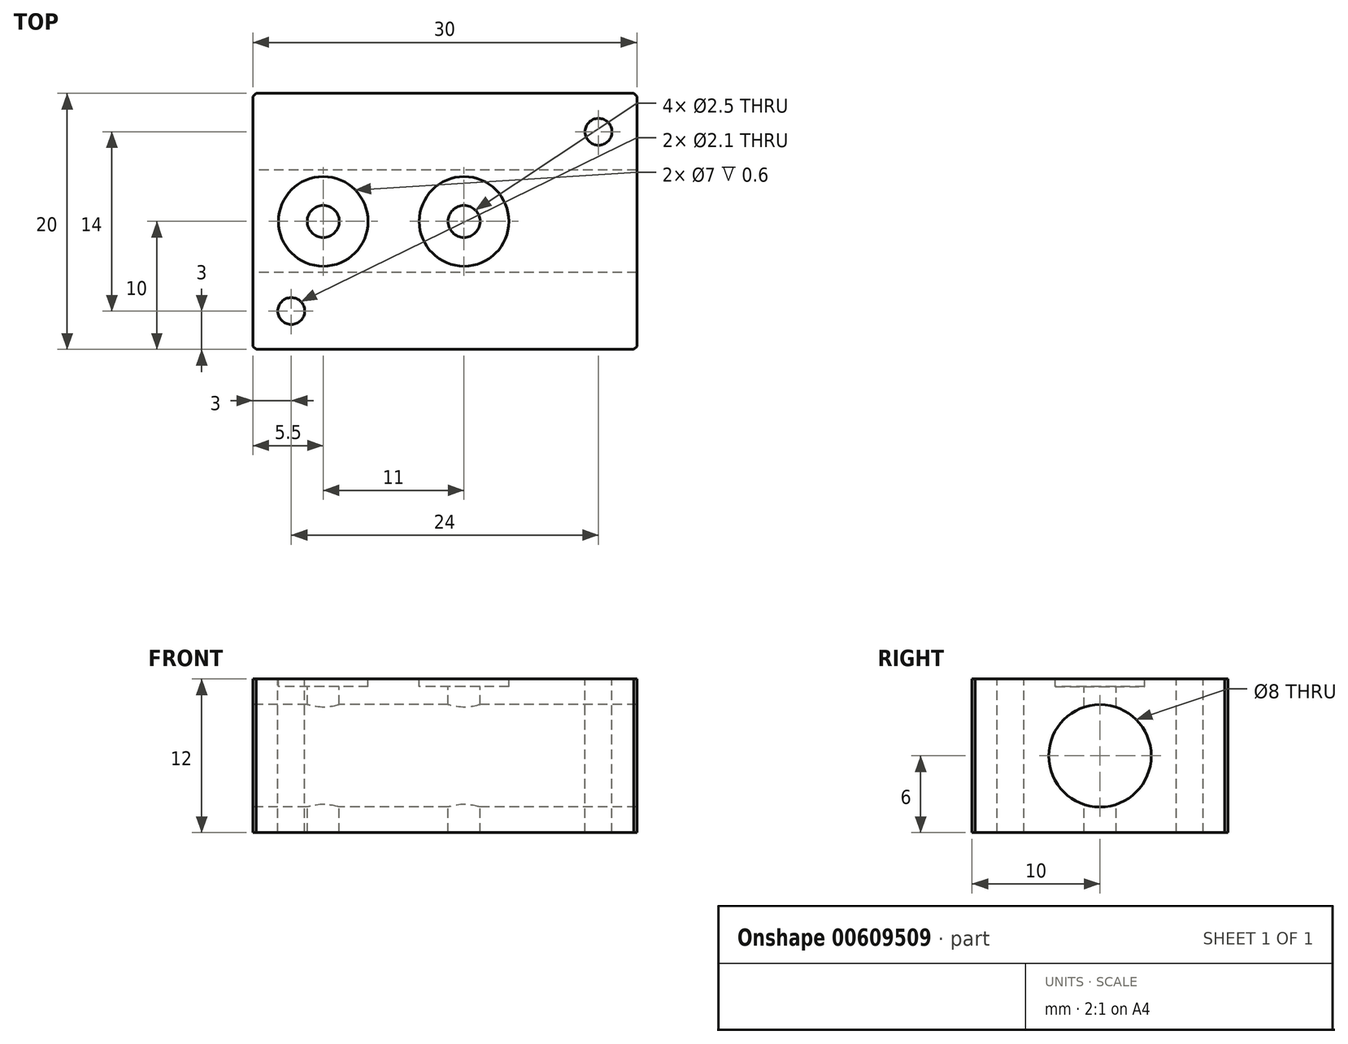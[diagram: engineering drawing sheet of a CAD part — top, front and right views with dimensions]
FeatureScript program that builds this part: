
annotation { "Feature Type Name" : "Feature", "Feature Type Description" : "" }
export const myFeature = defineFeature(function(context is Context, id is Id, definition is map)
    precondition{}
    {
        {
            var Q0;
            Q0=qCreatedBy(makeId("Top.planeOp"),FACE);
            var sketch = newSketch(context, id + "F0", { "sketchPlane" : qUnion([Q0])});
            skLineSegment(sketch, "E0.bottom", {"start": v(0, 0) * mm, "end": v(30, 0) * mm});
            skLineSegment(sketch, "E0.top", {"start": v(0, -20) * mm, "end": v(30, -20) * mm});
            skLineSegment(sketch, "E0.left", {"start": v(0, 0) * mm, "end": v(0, -20) * mm});
            skLineSegment(sketch, "E0.right", {"start": v(30, 0) * mm, "end": v(30, -20) * mm});
            skSolve(sketch);
        }
        {
            var Q0;
            Q0=makeQuery(id+"F0.imprint","IMPRINT",FACE,{"disambiguationData":[TD([[makeQuery(id+"F0.imprint","IMPRINT",EDGE,{"derivedFrom":sQuery(id+"F0.wireOp",EDGE,"E0.bottom")}),-1.0]])]});
            extrude(context, id + "F1", {"entities" : qUnion([Q0]), "depth" : 12 * mm, "offsetDistance" : 25 * mm});
        }
        {
            var Q0;
            Q0=makeQuery(id+"F1.opExtrude","SWEPT_FACE",FACE,{"disambiguationData":[OSD([sQuery(id+"F0.wireOp",EDGE,"E0.left")])]});
            var sketch = newSketch(context, id + "F2", { "sketchPlane" : qUnion([Q0])});
            skLineSegment(sketch, "E1", {"start": v(0, 6) * mm, "end": v(20, 6) * mm, "construction": true});
            skCircle(sketch, "E2", {"center": v(10, 6) * mm, "radius": 4 * mm});
            skSolve(sketch);
        }
        {
            var Q0;
            Q0=makeQuery(id+"F2.imprint","IMPRINT",FACE,{"disambiguationData":[TD([[makeQuery(id+"F2.imprint","IMPRINT",EDGE,{"derivedFrom":sQuery(id+"F2.wireOp",EDGE,"E2")}),1.0]])]});
            extrude(context, id + "F3", {"entities" : qUnion([Q0]), "operationType" : NewBodyOperationType.REMOVE, "oppositeDirection" : true, "depth" : 30 * mm, "offsetDistance" : 25 * mm});
        }
        {
            var Q0;
            Q0=makeQuery(id+"F1.opExtrude","CAP_FACE",FACE,{"disambiguationData":[OSD([sQuery(id+"F0.wireOp",EDGE,"E0.bottom"),sQuery(id+"F0.wireOp",EDGE,"E0.top"),sQuery(id+"F0.wireOp",EDGE,"E0.left"),sQuery(id+"F0.wireOp",EDGE,"E0.right")])],"isStart":false});
            var sketch = newSketch(context, id + "F4", { "sketchPlane" : qUnion([Q0])});
            skLineSegment(sketch, "E3", {"start": v(30, -10) * mm, "end": v(0, -10) * mm, "construction": true});
            skCircle(sketch, "E4", {"center": v(16.5, -10) * mm, "radius": 1.25 * mm});
            skCircle(sketch, "E5", {"center": v(5.5, -10) * mm, "radius": 1.25 * mm});
            skCircle(sketch, "E6", {"center": v(16.5, -10) * mm, "radius": 3.5 * mm});
            skCircle(sketch, "E7", {"center": v(5.5, -10) * mm, "radius": 3.5 * mm});
            skLineSegment(sketch, "E8", {"start": v(27, -20) * mm, "end": v(27, -3) * mm, "construction": true});
            skLineSegment(sketch, "E9", {"start": v(27, -3) * mm, "end": v(30, -3) * mm, "construction": true});
            skLineSegment(sketch, "E10", {"start": v(0, -17) * mm, "end": v(3, -17) * mm, "construction": true});
            skLineSegment(sketch, "E11", {"start": v(3, -17) * mm, "end": v(3, 0) * mm, "construction": true});
            skCircle(sketch, "E12", {"center": v(3, -17) * mm, "radius": 1.05 * mm});
            skCircle(sketch, "E13", {"center": v(27, -3) * mm, "radius": 1.05 * mm});
            skCircle(sketch, "E14", {"center": v(5.5, -10) * mm, "radius": 2.5 * mm});
            skCircle(sketch, "E15", {"center": v(16.5, -10) * mm, "radius": 2.5 * mm});
            skSolve(sketch);
        }
        {
            var Q0;
            Q0=makeQuery(id+"F4.imprint","IMPRINT",FACE,{"disambiguationData":[TD([[makeQuery(id+"F4.imprint","IMPRINT",EDGE,{"derivedFrom":sQuery(id+"F4.wireOp",EDGE,"E5")}),1.0]])]});
            var Q1;
            Q1=makeQuery(id+"F4.imprint","IMPRINT",FACE,{"disambiguationData":[TD([[makeQuery(id+"F4.imprint","IMPRINT",EDGE,{"derivedFrom":sQuery(id+"F4.wireOp",EDGE,"E4")}),1.0]])]});
            extrude(context, id + "F5", {"entities" : qUnion([Q0, Q1]), "operationType" : NewBodyOperationType.REMOVE, "oppositeDirection" : true, "depth" : 25 * mm, "offsetDistance" : 25 * mm});
        }
        {
            var Q0;
            Q0=makeQuery(id+"F1.opExtrude","CAP_FACE",FACE,{"disambiguationData":[OSD([sQuery(id+"F0.wireOp",EDGE,"E0.bottom"),sQuery(id+"F0.wireOp",EDGE,"E0.top"),sQuery(id+"F0.wireOp",EDGE,"E0.left"),sQuery(id+"F0.wireOp",EDGE,"E0.right")])],"isStart":true});
            var sketch = newSketch(context, id + "F6", { "sketchPlane" : qUnion([Q0])});
            skCircle(sketch, "E16", {"center": v(5.5, 10) * mm, "radius": 3 * mm});
            skCircle(sketch, "E17", {"center": v(16.5, 10) * mm, "radius": 3 * mm});
            skSolve(sketch);
        }
        {
            var Q0;
            Q0=makeQuery(id+"F1.opExtrude","CAP_FACE",FACE,{"disambiguationData":[OSD([sQuery(id+"F0.wireOp",EDGE,"E0.bottom"),sQuery(id+"F0.wireOp",EDGE,"E0.top"),sQuery(id+"F0.wireOp",EDGE,"E0.left"),sQuery(id+"F0.wireOp",EDGE,"E0.right")])],"isStart":true});
            var sketch = newSketch(context, id + "F7", { "sketchPlane" : qUnion([Q0])});
            skLineSegment(sketch, "E18.bottom", {"start": v(-8.36, -7.93) * mm, "end": v(37.73, -7.93) * mm});
            skLineSegment(sketch, "E18.top", {"start": v(-8.36, 26.65) * mm, "end": v(37.73, 26.65) * mm});
            skLineSegment(sketch, "E18.left", {"start": v(-8.36, -7.93) * mm, "end": v(-8.36, 26.65) * mm});
            skLineSegment(sketch, "E18.right", {"start": v(37.73, -7.93) * mm, "end": v(37.73, 26.65) * mm});
            skSolve(sketch);
        }
        {
            var Q0;
            Q0=makeQuery(id+"F4.imprint","IMPRINT",FACE,{"disambiguationData":[TD([[makeQuery(id+"F4.imprint","IMPRINT",EDGE,{"derivedFrom":sQuery(id+"F4.wireOp",EDGE,"E12")}),1.0]])]});
            var Q1;
            Q1=makeQuery(id+"F4.imprint","IMPRINT",FACE,{"disambiguationData":[TD([[makeQuery(id+"F4.imprint","IMPRINT",EDGE,{"derivedFrom":sQuery(id+"F4.wireOp",EDGE,"E13")}),1.0]])]});
            extrude(context, id + "F8", {"entities" : qUnion([Q0, Q1]), "operationType" : NewBodyOperationType.REMOVE, "oppositeDirection" : true, "depth" : 25 * mm, "offsetDistance" : 25 * mm});
        }
        {
            var Q0;
            Q0=makeQuery(id+"F3.boolean.opBoolean","COPY",EDGE,{"derivedFrom":makeQuery(id+"F3.opExtrude","CAP_EDGE",EDGE,{"disambiguationData":[OSD([sQuery(id+"F2.wireOp",EDGE,"E2")])],"isStart":true})});
            var Q1;
            Q1=makeQuery(id+"FJBm0b92ZMT9tFn_1.boolean.opBoolean","COPY",EDGE,{"derivedFrom":makeQuery(id+"FJBm0b92ZMT9tFn_1.opExtrude","CAP_EDGE",EDGE,{"disambiguationData":[OSD([sQuery(id+"FAXXHBaGUh8DWvs_1.wireOp",EDGE,"rXzBVNc6-XmbK-xtO8-ileB-jSKGWzc9BgFo")])],"isStart":true})});
            var Q2;
            Q2=makeQuery(id+"FJBm0b92ZMT9tFn_1.boolean.opBoolean","COPY",EDGE,{"derivedFrom":makeQuery(id+"FJBm0b92ZMT9tFn_1.opExtrude","CAP_EDGE",EDGE,{"disambiguationData":[OSD([sQuery(id+"FAXXHBaGUh8DWvs_1.wireOp",EDGE,"vd3QDH8B-I38S-UUpS-0Pry-Q9w0M2Qf0JR9")])],"isStart":true})});
            var Q3;
            Q3=makeQuery(id+"F9TEGv7PlH7K8f9_1.boolean.opBoolean","COPY",EDGE,{"derivedFrom":makeQuery(id+"F9TEGv7PlH7K8f9_1.opExtrude","CAP_EDGE",EDGE,{"disambiguationData":[OSD([sQuery(id+"FJbsTuyrFzBMji7_1.wireOp",EDGE,"w2qUx6aC-MVId-fWWE-JW74-3pC93mfXhfW8")])],"isStart":true})});
            var Q4;
            Q4=makeQuery(id+"F9TEGv7PlH7K8f9_1.boolean.opBoolean","COPY",EDGE,{"derivedFrom":makeQuery(id+"F9TEGv7PlH7K8f9_1.opExtrude","CAP_EDGE",EDGE,{"disambiguationData":[OSD([sQuery(id+"FJbsTuyrFzBMji7_1.wireOp",EDGE,"x6uTosDK-Su08-KXNi-5Ype-cPHAYPulsE8f")])],"isStart":true})});
            var Q5;
            Q5=makeQuery(id+"F1.opExtrude","SWEPT_EDGE",EDGE,{"disambiguationData":[OSD([sQuery(id+"F0.wireOp",EDGE,"E0.bottom"),sQuery(id+"F0.wireOp",EDGE,"E0.left")])]});
            var Q6;
            Q6=makeQuery(id+"F1.opExtrude","SWEPT_EDGE",EDGE,{"disambiguationData":[OSD([sQuery(id+"F0.wireOp",EDGE,"E0.top"),sQuery(id+"F0.wireOp",EDGE,"E0.left")])]});
            var Q7;
            Q7=makeQuery(id+"F1.opExtrude","SWEPT_EDGE",EDGE,{"disambiguationData":[OSD([sQuery(id+"F0.wireOp",EDGE,"E0.bottom"),sQuery(id+"F0.wireOp",EDGE,"E0.right")])]});
            var Q8;
            Q8=makeQuery(id+"F1.opExtrude","SWEPT_EDGE",EDGE,{"disambiguationData":[OSD([sQuery(id+"F0.wireOp",EDGE,"E0.top"),sQuery(id+"F0.wireOp",EDGE,"E0.right")])]});
            chamfer(context, id + "F9", {"entities" : qUnion([Q0, Q1, Q2, Q3, Q4, Q5, Q6, Q7, Q8]), "width" : 0.25 * mm, "tangentPropagation" : true});
        }
        {
            var Q0;
            Q0=makeQuery(id+"F4.imprint","IMPRINT",FACE,{"disambiguationData":[TD([[makeQuery(id+"F4.imprint","IMPRINT",EDGE,{"derivedFrom":sQuery(id+"F4.wireOp",EDGE,"E7")}),1.0]])]});
            var Q1;
            Q1=makeQuery(id+"F4.imprint","IMPRINT",FACE,{"disambiguationData":[TD([[makeQuery(id+"F4.imprint","IMPRINT",EDGE,{"derivedFrom":sQuery(id+"F4.wireOp",EDGE,"E6")}),1.0]])]});
            var Q2;
            Q2=makeQuery(id+"F4.imprint","IMPRINT",FACE,{"disambiguationData":[TD([[makeQuery(id+"F4.imprint","IMPRINT",EDGE,{"derivedFrom":sQuery(id+"F4.wireOp",EDGE,"E4")}),-1.0]])]});
            var Q3;
            Q3=makeQuery(id+"F4.imprint","IMPRINT",FACE,{"disambiguationData":[TD([[makeQuery(id+"F4.imprint","IMPRINT",EDGE,{"derivedFrom":sQuery(id+"F4.wireOp",EDGE,"E5")}),-1.0]])]});
            extrude(context, id + "F10", {"entities" : qUnion([Q0, Q1, Q2, Q3]), "operationType" : NewBodyOperationType.REMOVE, "oppositeDirection" : true, "depth" : .6 * mm, "offsetDistance" : 25 * mm});
        }
    });
